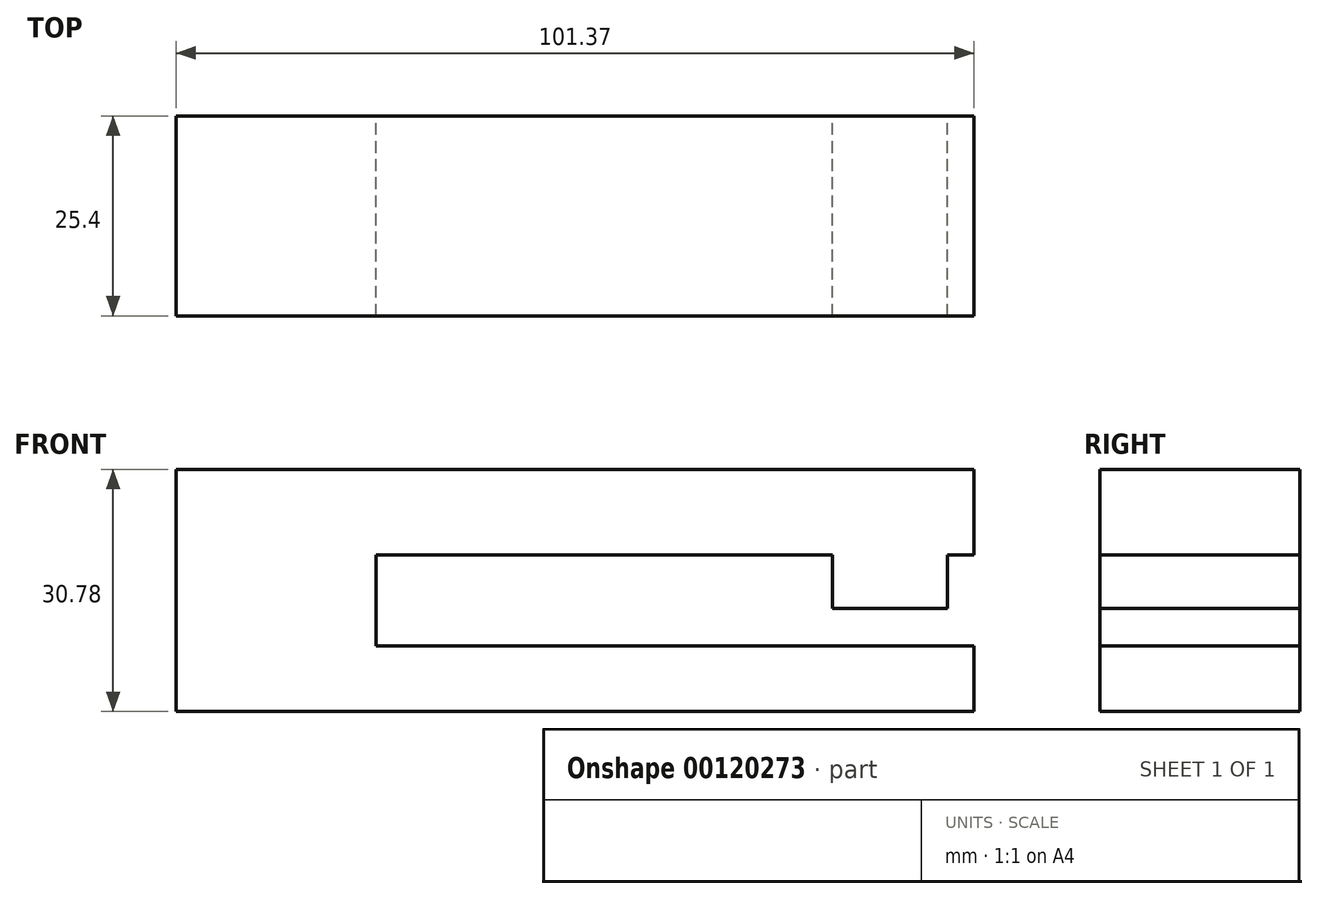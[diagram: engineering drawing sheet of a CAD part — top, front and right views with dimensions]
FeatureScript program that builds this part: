
annotation { "Feature Type Name" : "Feature", "Feature Type Description" : "" }
export const myFeature = defineFeature(function(context is Context, id is Id, definition is map)
    precondition{}
    {
        {
            var Q0;
            Q0=qCreatedBy(makeId("Front.planeOp"),FACE);
            var sketch = newSketch(context, id + "F0", { "sketchPlane" : qUnion([Q0])});
            skLineSegment(sketch, "E0.bottom", {"start": v(-49.01, 30.78) * mm, "end": v(52.36, 30.78) * mm});
            skLineSegment(sketch, "E0.top", {"start": v(-49.01, 19.9) * mm, "end": v(52.36, 19.9) * mm});
            skLineSegment(sketch, "E0.left", {"start": v(-49.01, 30.78) * mm, "end": v(-49.01, 19.9) * mm});
            skLineSegment(sketch, "E0.right", {"start": v(52.36, 30.78) * mm, "end": v(52.36, 19.9) * mm});
            skLineSegment(sketch, "E1", {"start": v(48.98, 21.4) * mm, "end": v(48.98, 13.14) * mm});
            skLineSegment(sketch, "E2", {"start": v(48.98, 13.14) * mm, "end": v(34.34, 13.14) * mm});
            skLineSegment(sketch, "E3", {"start": v(34.34, 13.14) * mm, "end": v(34.34, 19.9) * mm});
            skLineSegment(sketch, "E4.bottom", {"start": v(-49.01, 19.9) * mm, "end": v(-23.62, 19.9) * mm});
            skLineSegment(sketch, "E4.top", {"start": v(-49.01, 8.37) * mm, "end": v(-23.62, 8.37) * mm});
            skLineSegment(sketch, "E4.left", {"start": v(-49.01, 19.9) * mm, "end": v(-49.01, 8.37) * mm});
            skLineSegment(sketch, "E4.right", {"start": v(-23.62, 19.9) * mm, "end": v(-23.62, 8.37) * mm});
            skLineSegment(sketch, "E5.bottom", {"start": v(-49.01, 8.37) * mm, "end": v(52.32, 8.37) * mm});
            skLineSegment(sketch, "E5.top", {"start": v(-49.01, 0) * mm, "end": v(52.32, 0) * mm});
            skLineSegment(sketch, "E5.left", {"start": v(-49.01, 8.37) * mm, "end": v(-49.01, 0) * mm});
            skLineSegment(sketch, "E5.right", {"start": v(52.32, 8.37) * mm, "end": v(52.32, 0) * mm});
            skSolve(sketch);
        }
        {
            var Q0;
            Q0 = qSketchRegion(id + "F0", true);
            extrude(context, id + "F1", {"entities" : qUnion([Q0]), "depth" : 25.4 * mm});
        }
    });
